# Revit family: LIXIL - FJ2-100 N - COBRA FLUSH JUNIOR TOILET FLUSH VALVE
name_source: partatom
category: Plumbing Fixtures
units: mm (PartAtom-declared; Revit-internal decimal feet)

## family parameters
Always vertical = Yes
Cut with Voids When Loaded = No
Enable Cutting in Views = No
Maintain Annotation Orientation = No
OmniClass Number = 23.45.00.00
OmniClass Title = Sanitary, Laundry, and Cleaning Equipment
Part Type = Normal
Room Calculation Point = No
Round Connector Dimension = Use Diameter
Shared = Yes
Work Plane-Based = No

## types (1)
- FJ2-100 N
    DEPTH - 120MM MAX = 120 mm  [stored 0.393701 ft]
    Default Elevation = 0 mm  [stored 0 ft]
    Description = Cobra Flush Junior Toilet Flush Valve to detail and spec. See sanware schedule. Available from Lixil.
    HEIGHT - 675MM MAX = 580 mm  [stored 1.90289 ft]
    Hosted on lixil.co.za = https://www.lixil.co.za
    M _ FLUSH PIPE _ CHROME = M _ LIXIL - CHROME 01
    M _ FLUSH VALVE BODY = M _ LIXIL - CHROME 01
    M _ RUBBER _ BLACK _ SOFT = M _ LIXIL - RUBBER - BLACK 01
    Product Specification = Supplier: Lixil.
Product description: Junior Flushmaster exposed flush valve, chrome. Includes: back entry, flush pipe, rubber pan connector, wall flange, rubber seat buffer, integral vacuum breaker, and non-hold open feature.
Product Code: FFUUSBFJ-0GT01
SKU Code	: FJ2-100/N
Barcode: 6002194051428
Brand: Cobra
Range: Flush Junior
Category: Flush Valves
Sub-Category: Toilets
Colour: Chrome
Package Height: 80 mm
Package Width: 170 mm
Package Length: 690 mm
Package Volume: 9384000 mm³
Package Weight: 1.76 kg

Notes:
- Refer to manufacturer's and supplier's installation, maintenance and cleaning manual.
- Refer to manufacturer's and supplier's guarantees and warrantees document.

note: [stored X ft] marks values corroborated as IEEE doubles in the binary element streams (Revit-internal decimal feet)

## geometry (parser evidence)
native form markers: Sweep x13
no freeform markers — native parametric forms only
